# Revit family: vl-12(e)(r)k(h)(x)3_60Hz
name_source: partatom
category: 機械設備
units: mm (PartAtom-declared; Revit-internal decimal feet)

## family parameters
OmniClass タイトル = Centrifugal Fans
OmniClass 番号 = 23.75.35.17.27
パーツ タイプ = 標準
ロード時にボイドで切り取り = いいえ
丸型コネクタ寸法 = 直径を使用
作業面ベース = いいえ
共有 = いいえ
常に垂直 = はい
部屋計算ポイント = いいえ

## types (5) — shared parameters
Clearance Left = 150
Clearance Right = 150
Clearance Top = 150
Depth = 276  [stored 0.905512 ft]
Duct_H = 28
Duct_Pitch = 350  [stored 1.14829 ft]
EAサイズ_D = 75
Height = 298
IfcExportAs = IfcFanType
IfcExportType = CENTRIFUGALBACKWARDINCLINEDCURVED
MAX静圧 = 0.0 Pa
MID静圧 = 0.0 Pa
MID風量 = 0.0 m³/h
MIN静圧 = 0.0 Pa
OmniClassCode = 23-33 31 19 13 13
SAサイズ_D = 75
URL = https://www.mitsubishielectric.co.jp
Uniclass2015Code = Pr_65_67_29_89
Uniclass2015Title = Twin centrifugal fans
Uniclass2015Version = Systems v1.9
W2 = 148
Width = 295  [stored 0.967848 ft]
ダクト径 = 75 mm
マテリアル = 合成樹脂(白)
メンテナンススペース = はい
仕様書バージョン = Version1.0
企業コード = 108420
分類コード = 50052504100030
周波数 = 60 Hz
極数 = 2
法定耐用年数 = 15
相 = 1
積算_科目 = 2 換気設備
製品リリース年月 = 2019年5月16日
製品出荷対象 = 国内
製造元 = 三菱電機株式会社
設置方法 = 壁付
説明 = 換気空清機ロスナイ 準寒冷･温暖地仕様 壁埋込30cm角穴取付
負荷分類 = 3_ファン類
運転質量 = 0.00 kg
電動機出力 = 0 W
電圧 = 100 V
zero-valued in all types: Clearance Back, Clearance Bottom, Clearance Front

## per-type parameters (varying)
| type | D1 | H1 | MAX風量 | MIN風量 | W1 | 価格 | 消費電力 | 温度交換効率 | 製品質量 | 質量 |
| VL-12EKH3 | 25  [stored 0.082021 ft] | 346  [stored 1.13517 ft] | 57.0 m³/h | 0.0 m³/h | 354  [stored 1.16142 ft] | 55700 $ | 18 W | 65.00% | 4.50 kg | 5.40 kg |
| VL-12RKH3 | 25  [stored 0.082021 ft] | 346  [stored 1.13517 ft] | 57.0 m³/h | 0.0 m³/h | 354  [stored 1.16142 ft] | 63000 $ | 18 W | 65.00% | 4.50 kg | 5.40 kg |
| VL-12K3 | 25  [stored 0.082021 ft] | 346  [stored 1.13517 ft] | 100.0 m³/h | 60.0 m³/h | 354  [stored 1.16142 ft] | 53600 $ | 34 W | 55.00% | 4.50 kg | 5.40 kg |
| VL-12EK3 | 25  [stored 0.082021 ft] | 346  [stored 1.13517 ft] | 100.0 m³/h | 60.0 m³/h | 354  [stored 1.16142 ft] | 53600 $ | 34 W | 55.00% | 4.50 kg | 5.40 kg |
| VL-12EKX3 | 66 | 376 | 100.0 m³/h | 60.0 m³/h | 376 | 60200 $ | 34 W | 55.00% | 5.00 kg | 6.00 kg |

note: column(s) folded — value = type name in every type: モデル

note: [stored X ft] marks values corroborated as IEEE doubles in the binary element streams (Revit-internal decimal feet)
